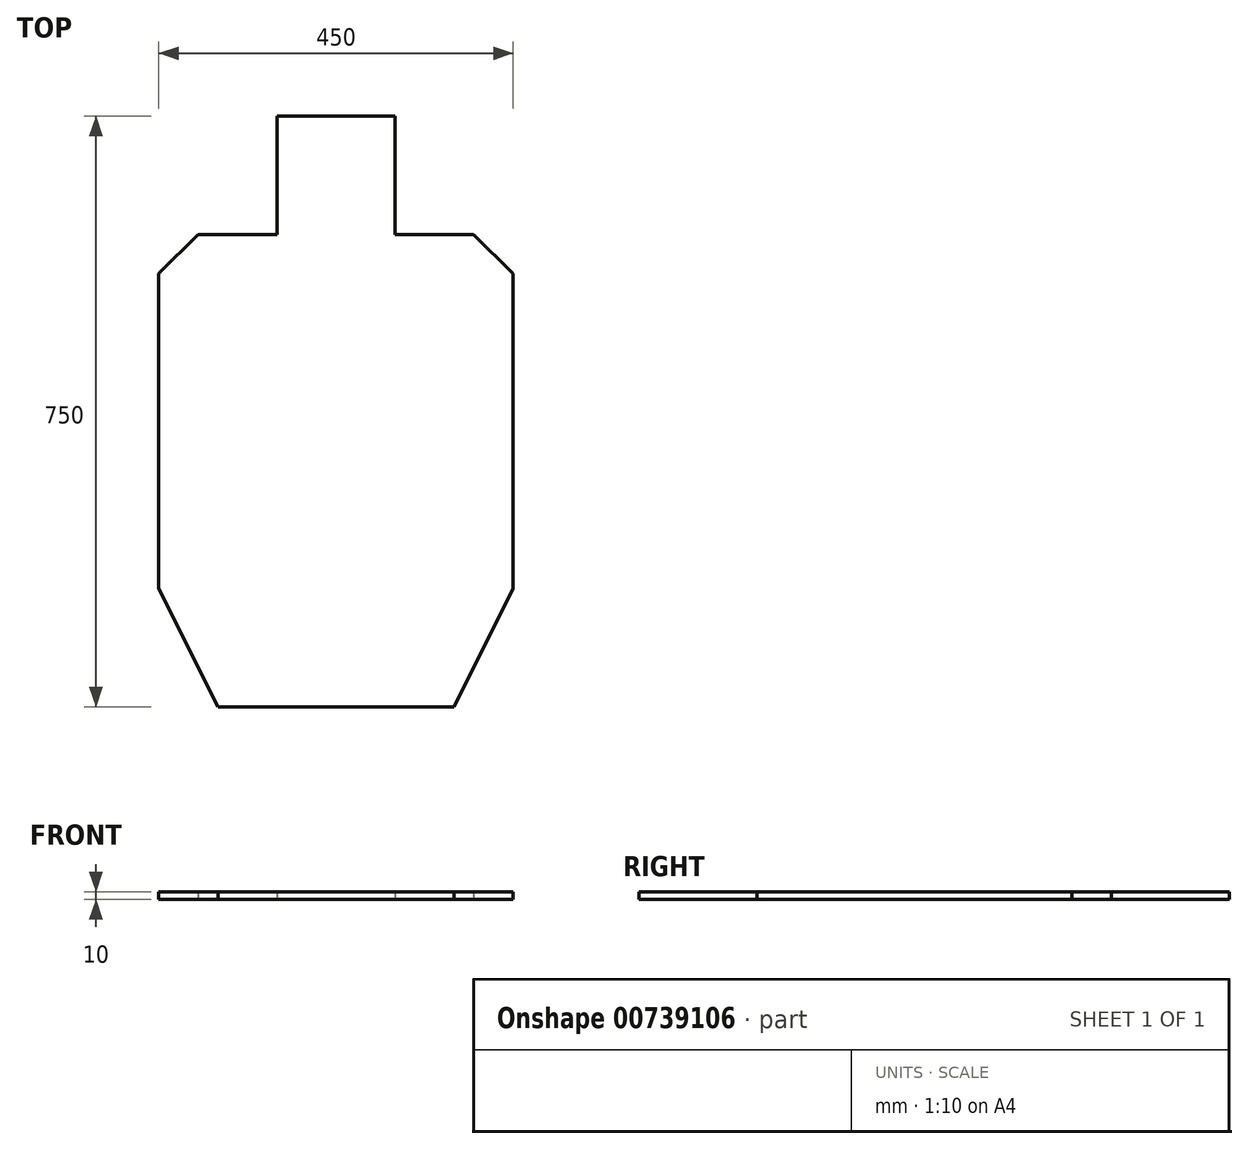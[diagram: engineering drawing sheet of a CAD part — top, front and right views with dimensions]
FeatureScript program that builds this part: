
annotation { "Feature Type Name" : "Feature", "Feature Type Description" : "" }
export const myFeature = defineFeature(function(context is Context, id is Id, definition is map)
    precondition{}
    {
        {
            var Q0;
            Q0=qCreatedBy(makeId("Top.planeOp"),FACE);
            var sketch = newSketch(context, id + "F0", { "sketchPlane" : qUnion([Q0])});
            skLineSegment(sketch, "E0", {"start": v(0, -364.58) * mm, "end": v(-150, -364.58) * mm});
            skLineSegment(sketch, "E1", {"start": v(-150, -364.58) * mm, "end": v(-225, -214.58) * mm});
            skLineSegment(sketch, "E2", {"start": v(-225, -214.58) * mm, "end": v(-225, 185.42) * mm});
            skLineSegment(sketch, "E3", {"start": v(-225, 185.42) * mm, "end": v(-175, 235.42) * mm});
            skLineSegment(sketch, "E4", {"start": v(-175, 235.42) * mm, "end": v(-75, 235.42) * mm});
            skLineSegment(sketch, "E5", {"start": v(-75, 235.42) * mm, "end": v(-75, 385.42) * mm});
            skLineSegment(sketch, "E6", {"start": v(-75, 385.42) * mm, "end": v(75, 385.42) * mm});
            skLineSegment(sketch, "E7", {"start": v(75, 385.42) * mm, "end": v(75, 235.42) * mm});
            skLineSegment(sketch, "E8", {"start": v(75, 235.42) * mm, "end": v(175, 235.42) * mm});
            skLineSegment(sketch, "E9", {"start": v(175, 235.42) * mm, "end": v(225, 185.42) * mm});
            skLineSegment(sketch, "E10", {"start": v(225, 185.42) * mm, "end": v(225, -214.58) * mm});
            skLineSegment(sketch, "E11", {"start": v(225, -214.58) * mm, "end": v(150, -364.58) * mm});
            skLineSegment(sketch, "E12", {"start": v(150, -364.58) * mm, "end": v(0, -364.58) * mm});
            skSolve(sketch);
        }
        {
            var Q0;
            Q0 = qSketchRegion(id + "F0", true);
            extrude(context, id + "F1", {"entities" : qUnion([Q0]), "depth" : 10 * mm, "offsetDistance" : 25 * mm});
        }
    });
